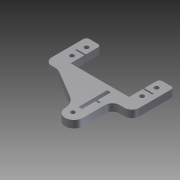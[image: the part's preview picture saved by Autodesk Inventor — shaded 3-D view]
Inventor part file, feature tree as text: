
AUTODESK INVENTOR PART (.ipt)
format: ipt  version: 2012 (Build 160160000, 160)  size: 189,952 bytes
history: native  units: mm
features: sketch x2, extrude x1, hole x1
ambient origin geometry x8: Origin, YZ Plane, XZ Plane, XY Plane, X Axis, Y Axis, Z Axis, Center Point
bodies: Solid1 (feature_tree)
feature tree (4):
  extrude  "Extrusion1"  [1 undecoded]
  hole  "Hole2"  [1 undecoded]
  sketch  "Sketch1"  dims[d14=5.0mm d15=0.0mm]
  sketch  "Sketch3"  dims[d59=1.25mm d60=2.5mm d61=19.8mm d62=5.0mm d63=9.4mm d64=2.5mm d65=1.0mm d66=1.0mm d67=1.0mm d68=5.0mm d69=10.0mm d70=10.0mm d71=2.0mm d81=40.0mm d82=40.0mm d83=10.0mm d84=10.0mm d88=6.75mm d89=1.25mm d90=2.5mm d91=19.8mm d92=5.0mm d93=9.4mm d94=2.5mm d95=1.0mm d96=1.0mm d97=1.0mm d98=5.0mm d99=10.0mm d100=10.0mm d101=2.0mm d102=10.0mm d103=10.0mm d104=4.5mm d105=4.5mm d106=4.5mm d107=4.5mm d108=4.0mm d109=48.0mm d110=48.0mm d111=40.0mm d112=40.0mm d113=10.0mm d114=10.0mm d115=4.0mm d116=4.0mm d117=4.0mm d118=6.75mm d119=3.0mm d120=6.0mm d121=4.0mm d122=2.0mm d123=90.0deg d124=8.0mm d125=20.594885mm]
note: 2 required parameter values undecoded (feature->parameter linkage not recoverable at this tier; creation-order binding heuristic only, values carry confidence <= 0.55)
